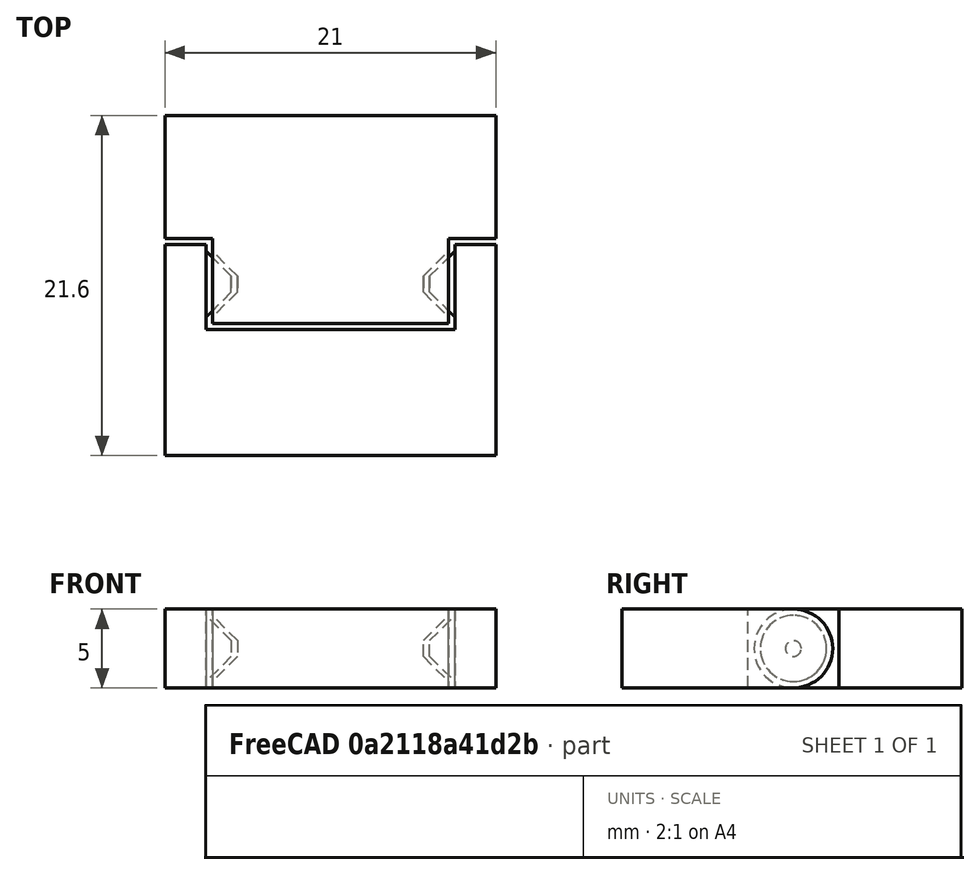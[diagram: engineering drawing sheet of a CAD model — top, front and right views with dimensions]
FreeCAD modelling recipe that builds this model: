
FCSTD DOCUMENT  (FreeCAD 1.0R1.0.1)
Label: PrintInPlace01
License: All rights reserved
LicenseURL: http://en.wikipedia.org/wiki/All_rights_reserved
objects: Part::Box×4, Part::MultiFuse×4, Part::Cone×4, Part::Cylinder×2, Part::Cut×2, Spreadsheet::Sheet×1
note: 16 computed .brp shape members not serialized (recipe doc carries the construction recipe); baked Part::Feature solids carry a one-line shape summary decoded from their .brp

FEATURE [Part::Box] Box  label="Cube"
  AttacherType = Attacher::AttachEngine3D
  Height = 5
  Length = 21
  Width = 10.9
  expr: Height = <<HingeParams>>.thickness
  expr: Length = <<HingeParams>>.h1 + <<HingeParams>>.h2
  expr: Width = <<HingeParams>>.e1 + <<HingeParams>>.thickness / 2 + <<HingeParams>>.gap
FEATURE [Spreadsheet::Sheet] Spreadsheet  label="HingeParams"
  cells = A2='Thickness; B2(thickness)=5; A3='Hinge length 1; B3(h1)=15; A4='Hinge length 2; B4(h2)=6; A5='Gap; B5(gap)=0.4; A6='Extend 1; B6(e1)=8; A7='Extend 2; B7(e2)=8
FEATURE [Part::Cylinder] Cylinder
  Angle = 360
  AttacherType = Attacher::AttachEngine3D
  FirstAngle = 0
  Height = 21
  Placement = pos=(0,10.9,2.5) rot=(0,1,0;1.5708rad)
  Radius = 2.5
  SecondAngle = 0
  expr: .Placement.Base.y = <<HingeParams>>.e1 + <<HingeParams>>.gap + <<HingeParams>>.thickness / 2
  expr: .Placement.Base.z = <<HingeParams>>.thickness / 2
  expr: Height = <<HingeParams>>.h1 + <<HingeParams>>.h2
  expr: Radius = <<HingeParams>>.thickness / 2
FEATURE [Part::Box] Box001  label="Cube001"
  AttacherType = Attacher::AttachEngine3D
  Height = 5
  Length = 15.8
  Placement = pos=(2.6,8,0) rot=(0,0,1;0rad)
  Width = 5.8
  expr: .Placement.Base.x = <<HingeParams>>.h2 / 2 - <<HingeParams>>.gap
  expr: .Placement.Base.y = <<HingeParams>>.e1
  expr: Height = <<HingeParams>>.thickness
  expr: Length = <<HingeParams>>.h1 + 2 * <<HingeParams>>.gap
  expr: Width = <<HingeParams>>.thickness + 2 * <<HingeParams>>.gap
FEATURE [Part::MultiFuse] Fusion
  Shapes = -> [Box,Cylinder]
FEATURE [Part::Cut] Cut
  Base = -> Fusion
  Tool = -> Box001
FEATURE [Part::Cone] Cone
  Angle = 360
  AttacherType = Attacher::AttachEngine3D
  Height = 1.6
  Placement = pos=(4.2,10.9,2.5) rot=(0,1,0;-1.5708rad)
  Radius1 = 0.5
  Radius2 = 2.1
  expr: .Placement.Base.x = <<HingeParams>>.h2 / 2 - <<HingeParams>>.gap + <<HingeParams>>.thickness / 2 - <<HingeParams>>.gap - 0.5
  expr: .Placement.Base.y = <<HingeParams>>.e1 + <<HingeParams>>.gap + <<HingeParams>>.thickness / 2
  expr: .Placement.Base.z = <<HingeParams>>.thickness / 2
  expr: Height = <<HingeParams>>.thickness / 2 - <<HingeParams>>.gap - 0.5
  expr: Radius1 = 0.5
  expr: Radius2 = <<HingeParams>>.thickness / 2 - <<HingeParams>>.gap
FEATURE [Part::Cone] Cone002
  Angle = 360
  AttacherType = Attacher::AttachEngine3D
  Height = 2
  Placement = pos=(4.6,10.9,2.5) rot=(0,1,0;-1.5708rad)
  Radius1 = 0.5
  Radius2 = 2.5
  expr: .Placement.Base.x = <<HingeParams>>.h2 / 2 + <<HingeParams>>.thickness / 2 - <<HingeParams>>.gap - 0.5
  expr: .Placement.Base.y = <<HingeParams>>.e1 + <<HingeParams>>.gap + <<HingeParams>>.thickness / 2
  expr: .Placement.Base.z = <<HingeParams>>.thickness / 2
  expr: Height = <<HingeParams>>.thickness / 2 - 0.5
  expr: Radius1 = 0.5
  expr: Radius2 = <<HingeParams>>.thickness / 2
FEATURE [Part::Cone] Cone003
  Angle = 360
  AttacherType = Attacher::AttachEngine3D
  Height = 1.6
  Placement = pos=(16.8,10.9,2.5) rot=(0,1,0;1.5708rad)
  Radius1 = 0.5
  Radius2 = 2.1
  expr: .Placement.Base.x = <<HingeParams>>.h1 + <<HingeParams>>.h2 / 2 - (<<HingeParams>>.thickness / 2 - <<HingeParams>>.gap - 0.5) + <<HingeParams>>.gap
  expr: .Placement.Base.y = <<HingeParams>>.e1 + <<HingeParams>>.gap + <<HingeParams>>.thickness / 2
  expr: .Placement.Base.z = <<HingeParams>>.thickness / 2
  expr: Height = <<HingeParams>>.thickness / 2 - <<HingeParams>>.gap - 0.5
  expr: Radius1 = 0.5
  expr: Radius2 = <<HingeParams>>.thickness / 2 - <<HingeParams>>.gap
FEATURE [Part::Cone] Cone004
  Angle = 360
  AttacherType = Attacher::AttachEngine3D
  Height = 2
  Placement = pos=(16.4,10.9,2.5) rot=(0,1,0;1.5708rad)
  Radius1 = 0.5
  Radius2 = 2.5
  expr: .Placement.Base.x = <<HingeParams>>.h1 + <<HingeParams>>.h2 / 2 - (<<HingeParams>>.thickness / 2 - <<HingeParams>>.gap - 0.5)
  expr: .Placement.Base.y = <<HingeParams>>.e1 + <<HingeParams>>.gap + <<HingeParams>>.thickness / 2
  expr: .Placement.Base.z = <<HingeParams>>.thickness / 2
  expr: Height = <<HingeParams>>.thickness / 2 - 0.5
  expr: Radius1 = 0.5
  expr: Radius2 = <<HingeParams>>.thickness / 2
FEATURE [Part::MultiFuse] Fusion001
  Shapes = -> [Cone,Cone003,Cut]
FEATURE [Part::Cylinder] Cylinder001
  Angle = 360
  AttacherType = Attacher::AttachEngine3D
  FirstAngle = 0
  Height = 15
  Placement = pos=(3,10.9,2.5) rot=(0,1,0;1.5708rad)
  Radius = 2.5
  SecondAngle = 0
  expr: .Placement.Base.x = <<HingeParams>>.h2 / 2
  expr: .Placement.Base.y = <<HingeParams>>.e1 + <<HingeParams>>.gap + <<HingeParams>>.thickness / 2
  expr: .Placement.Base.z = <<HingeParams>>.thickness / 2
  expr: Height = <<HingeParams>>.h1
  expr: Radius = <<HingeParams>>.thickness / 2
FEATURE [Part::Box] Box002  label="Cube002"
  AttacherType = Attacher::AttachEngine3D
  Height = 5
  Length = 15
  Placement = pos=(3,10.9,0) rot=(0,0,1;0rad)
  Width = 10.5
  expr: .Placement.Base.x = <<HingeParams>>.h2 / 2
  expr: .Placement.Base.y = <<HingeParams>>.e1 + <<HingeParams>>.gap + <<HingeParams>>.thickness / 2
  expr: Height = <<HingeParams>>.thickness
  expr: Length = <<HingeParams>>.h1
  expr: Width = <<HingeParams>>.thickness / 2 + <<HingeParams>>.e2
FEATURE [Part::Box] Box003  label="Cube003"
  AttacherType = Attacher::AttachEngine3D
  Height = 5
  Length = 21
  Placement = pos=(0,13.8,0) rot=(0,0,1;0rad)
  Width = 7.8
  expr: .Placement.Base.y = <<HingeParams>>.e1 + <<HingeParams>>.thickness + <<HingeParams>>.gap * 2
  expr: Height = <<HingeParams>>.thickness
  expr: Length = <<HingeParams>>.h1 + <<HingeParams>>.h2
  expr: Width = <<HingeParams>>.e2 - <<HingeParams>>.gap / 2
FEATURE [Part::MultiFuse] Fusion002
  Shapes = -> [Box003,Box002,Cylinder001]
FEATURE [Part::MultiFuse] Fusion003
  Shapes = -> [Cone004,Cone002]
FEATURE [Part::Cut] Cut001
  Base = -> Fusion002
  Tool = -> Fusion003
